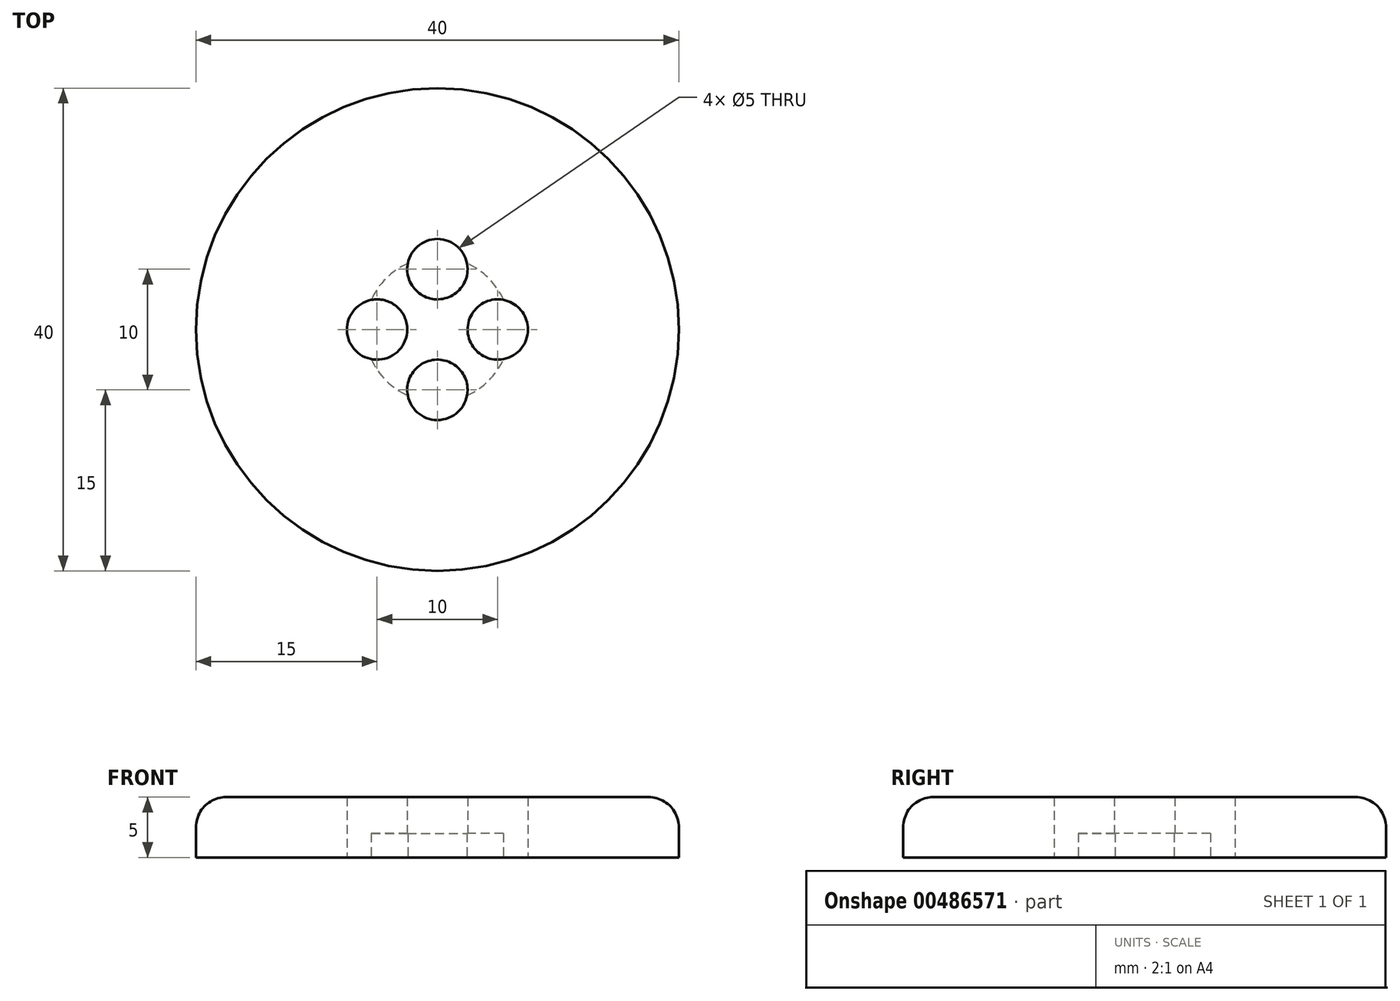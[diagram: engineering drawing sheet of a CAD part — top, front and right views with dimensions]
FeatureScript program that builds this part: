
annotation { "Feature Type Name" : "Feature", "Feature Type Description" : "" }
export const myFeature = defineFeature(function(context is Context, id is Id, definition is map)
    precondition{}
    {
        {
            var Q0;
            Q0=qCreatedBy(makeId("Top.planeOp"),FACE);
            var sketch = newSketch(context, id + "F0", { "sketchPlane" : qUnion([Q0])});
            skCircle(sketch, "E0", {"center": v(0, 0) * mm, "radius": 20 * mm});
            skSolve(sketch);
        }
        {
            var Q0;
            Q0=makeQuery(id+"F0.imprint","IMPRINT",FACE,{"disambiguationData":[TD([[makeQuery(id+"F0.imprint","IMPRINT",EDGE,{"derivedFrom":sQuery(id+"F0.wireOp",EDGE,"F2yPvgMP-rn7X-R1T2-pQRa-HH5yYNCkzPzg")}),1.0]])]});
            var Q1;
            Q1=makeQuery(id+"F0.imprint","IMPRINT",FACE,{"disambiguationData":[TD([[makeQuery(id+"F0.imprint","IMPRINT",EDGE,{"derivedFrom":sQuery(id+"F0.wireOp",EDGE,"E0")}),1.0]])]});
            extrude(context, id + "F1", {"entities" : qUnion([Q0, Q1]), "depth" : 5 * mm});
        }
        {
            var Q0;
            Q0=makeQuery(id+"F1.opExtrude","CAP_EDGE",EDGE,{"disambiguationData":[OSD([sQuery(id+"F0.wireOp",EDGE,"E0")])],"isStart":false});
            fillet(context, id + "F2", {"entities" : qUnion([Q0]), "radius" : 2.5 * mm, "tangentPropagation" : true, "allowEdgeOverflow" : false});
        }
        {
            var Q0;
            Q0=qCreatedBy(makeId("Top.planeOp"),FACE);
            var sketch = newSketch(context, id + "F3", { "sketchPlane" : qUnion([Q0])});
            skLineSegment(sketch, "E1", {"start": v(0, 0) * mm, "end": v(5, 0) * mm});
            skLineSegment(sketch, "E2", {"start": v(5, 0) * mm, "end": v(0, 0) * mm});
            skLineSegment(sketch, "E3", {"start": v(0, -5) * mm, "end": v(0, 0) * mm});
            skLineSegment(sketch, "E4", {"start": v(-5, 0) * mm, "end": v(0, 0) * mm});
            skLineSegment(sketch, "E5", {"start": v(0, 0) * mm, "end": v(0, 5) * mm});
            skCircle(sketch, "E6", {"center": v(0, -5) * mm, "radius": 2.5 * mm});
            skCircle(sketch, "E7", {"center": v(5, 0) * mm, "radius": 2.5 * mm});
            skCircle(sketch, "E8", {"center": v(0, 5) * mm, "radius": 2.5 * mm});
            skCircle(sketch, "E9", {"center": v(-5, 0) * mm, "radius": 2.5 * mm});
            skSolve(sketch);
        }
        {
            var Q0;
            Q0=makeQuery(id+"F3.imprint","IMPRINT",FACE,{"disambiguationData":[TD([[makeQuery(id+"F3.imprint","IMPRINT",EDGE,{"derivedFrom":sQuery(id+"F3.wireOp",EDGE,"E8")}),1.0]])]});
            var Q1;
            Q1=makeQuery(id+"F3.imprint","IMPRINT",FACE,{"disambiguationData":[TD([[makeQuery(id+"F3.imprint","IMPRINT",EDGE,{"derivedFrom":sQuery(id+"F3.wireOp",EDGE,"E9")}),1.0]])]});
            var Q2;
            Q2=makeQuery(id+"F3.imprint","IMPRINT",FACE,{"disambiguationData":[TD([[makeQuery(id+"F3.imprint","IMPRINT",EDGE,{"derivedFrom":sQuery(id+"F3.wireOp",EDGE,"E6")}),1.0]])]});
            var Q3;
            Q3=makeQuery(id+"F3.imprint","IMPRINT",FACE,{"disambiguationData":[TD([[makeQuery(id+"F3.imprint","IMPRINT",EDGE,{"derivedFrom":sQuery(id+"F3.wireOp",EDGE,"E7")}),1.0]])]});
            extrude(context, id + "F4", {"entities" : qUnion([Q0, Q1, Q2, Q3]), "operationType" : NewBodyOperationType.REMOVE, "depth" : 25 * mm});
        }
        {
            var Q0;
            Q0=qCreatedBy(makeId("Top.planeOp"),FACE);
            var sketch = newSketch(context, id + "F5", { "sketchPlane" : qUnion([Q0])});
            skCircle(sketch, "E10", {"center": v(0, 0) * mm, "radius": 6 * mm});
            skSolve(sketch);
        }
        {
            var Q0;
            Q0=makeQuery(id+"F5.imprint","IMPRINT",FACE,{"disambiguationData":[TD([[makeQuery(id+"F5.imprint","IMPRINT",EDGE,{"derivedFrom":sQuery(id+"F5.wireOp",EDGE,"E10")}),1.0]])]});
            extrude(context, id + "F6", {"entities" : qUnion([Q0]), "operationType" : NewBodyOperationType.REMOVE, "depth" : 2 * mm});
        }
    });
